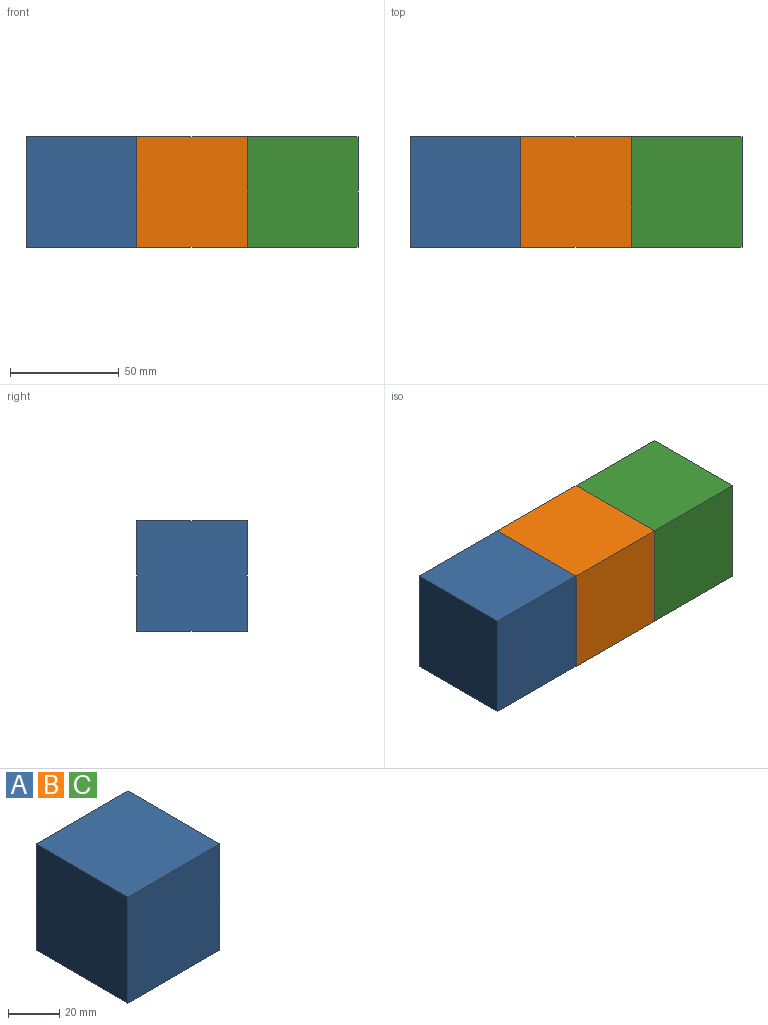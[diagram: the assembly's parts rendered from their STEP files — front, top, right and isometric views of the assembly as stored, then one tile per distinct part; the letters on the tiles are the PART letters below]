
ASSEMBLY  parts=3 mates=1
PART A: 6 faces, bbox 50.8x50.8x50.8 mm
  f0: plane 50.8x50.8mm, normal (1,0,0), area 2580.6mm2, adj f1,f3,f4,f5
  f1: plane 50.8x50.8mm, normal (0,0,1), area 2580.6mm2, adj f0,f2,f4,f5
  f2: plane 50.8x50.8mm, normal (-1,0,0), area 2580.6mm2, adj f1,f3,f4,f5
  f3: plane 50.8x50.8mm, normal (0,0,-1), area 2580.6mm2, adj f0,f2,f4,f5
  f4: plane 50.8x50.8mm, normal (0,1,0), area 2580.6mm2, adj f0,f1,f2,f3
  f5: plane 50.8x50.8mm, normal (0,-1,0), area 2580.6mm2, adj f0,f1,f2,f3
PART B: same geometry as A
PART C: same geometry as A
PLACE A t=(-50.45,3.81,-65.05)mm
PLACE B t=(0.35,3.81,-65.05)mm
PLACE C t=(51.15,3.81,-65.05)mm
MATE fastened A.f0 <-> B.f2  axis (1,0,0) through (-25.05,29.21,-65.05)mm
